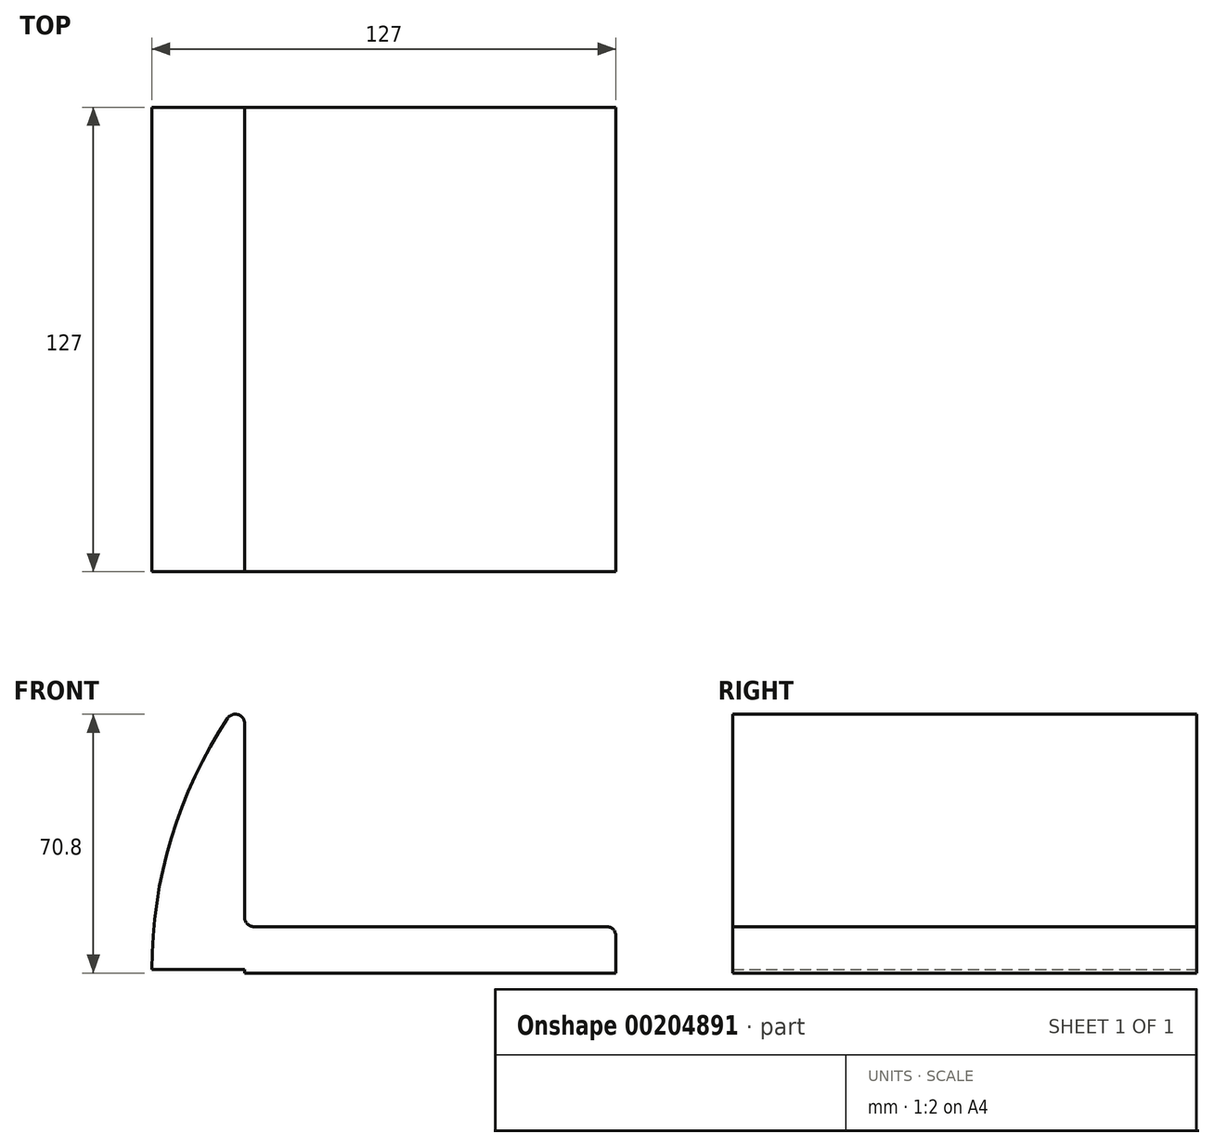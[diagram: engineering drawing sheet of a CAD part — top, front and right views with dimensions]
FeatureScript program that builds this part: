
annotation { "Feature Type Name" : "Feature", "Feature Type Description" : "" }
export const myFeature = defineFeature(function(context is Context, id is Id, definition is map)
    precondition{}
    {
        {
            var Q0;
            Q0=qCreatedBy(makeId("Front.planeOp"),FACE);
            var sketch = newSketch(context, id + "F0", { "sketchPlane" : qUnion([Q0])});
            skLineSegment(sketch, "E0", {"start": v(0, 1.02) * mm, "end": v(25.4, 1.02) * mm});
            skLineSegment(sketch, "E1", {"start": v(25.4, 1.02) * mm, "end": v(25.4, 0) * mm});
            skLineSegment(sketch, "E2", {"start": v(25.4, 0) * mm, "end": v(127, 0) * mm});
            skLineSegment(sketch, "E3", {"start": v(127, 0) * mm, "end": v(127, 12.7) * mm});
            skLineSegment(sketch, "E4", {"start": v(127, 12.7) * mm, "end": v(25.4, 12.7) * mm});
            skArc(sketch, "E5", {"start": v(0, 1.02) * mm, "mid": v(6.52, 40.7) * mm, "end": v(25.4, 76.2) * mm});
            skLineSegment(sketch, "E6", {"start": v(25.4, 76.2) * mm, "end": v(25.4, 12.7) * mm});
            skSolve(sketch);
        }
        {
            var Q0;
            Q0=makeQuery(id+"F0.imprint","IMPRINT",FACE,{"disambiguationData":[TD([[makeQuery(id+"F0.imprint","IMPRINT",EDGE,{"derivedFrom":sQuery(id+"F0.wireOp",EDGE,"E0")}),1.0]])]});
            extrude(context, id + "F1", {"entities" : qUnion([Q0]), "depth" : 127 * mm});
        }
        {
            var Q0;
            Q0=makeQuery(id+"F1.opExtrude","SWEPT_EDGE",EDGE,{"disambiguationData":[OSD([sQuery(id+"F0.wireOp",EDGE,"E5"),sQuery(id+"F0.wireOp",EDGE,"E6")])]});
            var Q1;
            Q1=makeQuery(id+"F1.opExtrude","SWEPT_EDGE",EDGE,{"disambiguationData":[OSD([sQuery(id+"F0.wireOp",EDGE,"E4"),sQuery(id+"F0.wireOp",EDGE,"E6")])]});
            var Q2;
            Q2=makeQuery(id+"F1.opExtrude","SWEPT_EDGE",EDGE,{"disambiguationData":[OSD([sQuery(id+"F0.wireOp",EDGE,"E3"),sQuery(id+"F0.wireOp",EDGE,"E4")])]});
            fillet(context, id + "F2", {"entities" : qUnion([Q0, Q1, Q2]), "radius" : 2.54 * mm, "tangentPropagation" : true, "allowEdgeOverflow" : false});
        }
    });
